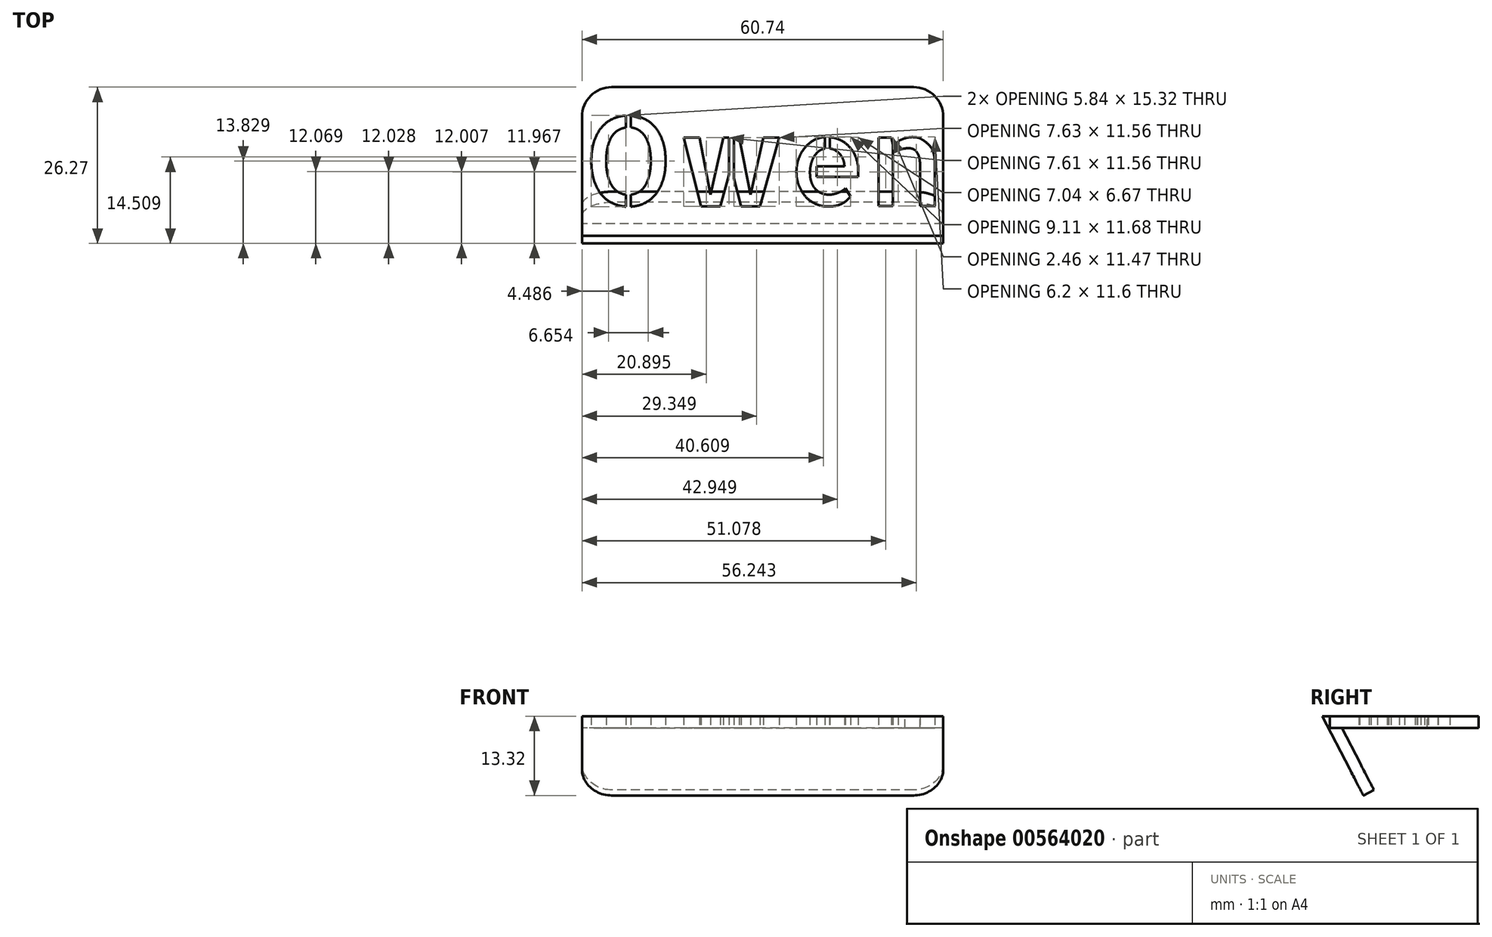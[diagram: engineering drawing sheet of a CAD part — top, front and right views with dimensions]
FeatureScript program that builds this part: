
annotation { "Feature Type Name" : "Feature", "Feature Type Description" : "" }
export const myFeature = defineFeature(function(context is Context, id is Id, definition is map)
    precondition{}
    {
        {
            var Q0;
            Q0=qCreatedBy(makeId("Top.planeOp"),FACE);
            var sketch = newSketch(context, id + "F0", { "sketchPlane" : qUnion([Q0])});
            skLineSegment(sketch, "E0.bottom", {"start": v(-23.58, 12.5) * mm, "end": v(37.16, 12.5) * mm});
            skLineSegment(sketch, "E0.top", {"start": v(-23.58, -12.5) * mm, "end": v(37.16, -12.5) * mm});
            skLineSegment(sketch, "E0.left", {"start": v(-23.58, 12.5) * mm, "end": v(-23.58, -12.5) * mm});
            skLineSegment(sketch, "E0.right", {"start": v(37.16, 12.5) * mm, "end": v(37.16, -12.5) * mm});
            skText(sketch, "E1", { "text": "Owen", "fontName": "AllertaStencil-Regular.ttf"});
            const initialGuessF0  = {"E1": [-0.02358, -0.0075, 1, 0, 0.015]};
            skSetInitialGuess(sketch, initialGuessF0);
            skSolve(sketch);
        }
        {
            var Q0;
            Q0=makeQuery(id+"F0.imprint","IMPRINT",FACE,{"disambiguationData":[TD([[makeQuery(id+"F0.imprint","IMPRINT",EDGE,{"derivedFrom":sQuery(id+"F0.wireOp",EDGE,"E0.bottom")}),-1.0]])]});
            extrude(context, id + "F1", {"entities" : qUnion([Q0]), "depth" : 2 * mm, "offsetDistance" : 25 * mm});
        }
        {
            var Q0;
            {var subQ0=sQuery(id+"F0.wireOp",EDGE,"E0.left");Q0=makeQuery(id+"FYEOEdhl7jzHk82_2.opBoolean","MERGE",FACE,{"derivedFrom":[makeQuery(id+"F1.opExtrude","SWEPT_FACE",FACE,{"disambiguationData":[OSD([subQ0])]}),makeQuery(id+"FOv1BJgTRWeWuMw_1.opExtrude","CAP_FACE",FACE,{"disambiguationData":[OSD([sQuery(id+"F0.wireOp",EDGE,"E0.bottom"),subQ0,sQuery(id+"Fjco5yBOxZZxTCI_1.wireOp",EDGE,"TpTMtmOo-qoIM-rLEy-p7IH-mKgsBanMGF23"),sQuery(id+"Fjco5yBOxZZxTCI_1.wireOp",EDGE,"Ja6BvVoQ-cpFi-Lcom-cL8s-5xC4kZiynyNl"),sQuery(id+"Fjco5yBOxZZxTCI_1.wireOp",EDGE,"utNyaJ8P-FD6r-AD7x-tpFW-fHytfVhziHLl"),sQuery(id+"Fjco5yBOxZZxTCI_1.wireOp",EDGE,"xGzW29bi-H5H8-ObLh-gdKj-mSPkAtMAUUzO")])],"isStart":true})]});}
            var sketch = newSketch(context, id + "F2", { "sketchPlane" : qUnion([Q0])});
            skLineSegment(sketch, "E2", {"start": v(11.52, 2) * mm, "end": v(5.09, -10.4) * mm});
            skLineSegment(sketch, "E3", {"start": v(5.09, -10.4) * mm, "end": v(6.87, -11.32) * mm});
            skLineSegment(sketch, "E4", {"start": v(6.87, -11.32) * mm, "end": v(13.77, 2) * mm});
            skLineSegment(sketch, "E5", {"start": v(13.77, 2) * mm, "end": v(11.52, 2) * mm});
            skSolve(sketch);
        }
        {
            var Q0;
            {var subQ4=sQuery(id+"F2.wireOp",EDGE,"E3");Q0=makeQuery(id+"F2.imprint","IMPRINT",FACE,{"disambiguationData":[TD([[makeQuery(id+"F2.imprint","IMPRINT",EDGE,{"derivedFrom":subQ4}),1.0]])]});}
            var Q1;
            Q1=makeQuery(id+"F1.opExtrude","SWEPT_FACE",FACE,{"disambiguationData":[OSD([sQuery(id+"F0.wireOp",EDGE,"E0.right")])]});
            extrude(context, id + "F3", {"entities" : qUnion([Q0]), "endBound" : BoundingType.UP_TO_SURFACE, "oppositeDirection" : true, "depth" : 75 * mm, "endBoundEntityFace" : qUnion([Q1]), "offsetDistance" : 25 * mm});
        }
        {
            var Q0;
            Q0=makeQuery(id+"F1.opExtrude","SWEPT_EDGE",EDGE,{"disambiguationData":[OSD([sQuery(id+"F0.wireOp",EDGE,"E0.bottom"),sQuery(id+"F0.wireOp",EDGE,"E0.left")])]});
            var Q1;
            Q1=makeQuery(id+"F1.opExtrude","SWEPT_EDGE",EDGE,{"disambiguationData":[OSD([sQuery(id+"F0.wireOp",EDGE,"E0.bottom"),sQuery(id+"F0.wireOp",EDGE,"E0.right")])]});
            var Q2;
            Q2=makeQuery(id+"F3.opExtrude","CAP_EDGE",EDGE,{"disambiguationData":[OSD([sQuery(id+"F2.wireOp",EDGE,"E3")])],"isStart":false});
            var Q3;
            Q3=makeQuery(id+"F3.opExtrude","CAP_EDGE",EDGE,{"disambiguationData":[OSD([sQuery(id+"F2.wireOp",EDGE,"E3")])],"isStart":true});
            var Q4;
            Q4=makeQuery(id+"F3.opExtrude","TWEAK_EDGE",EDGE,{"derivedFrom":[makeQuery(id+"F1.opExtrude","SWEPT_FACE",FACE,{"disambiguationData":[OSD([sQuery(id+"F0.wireOp",EDGE,"E0.right")])]}),makeQuery(id+"F2.imprint","IMPRINT",EDGE,{"derivedFrom":sQuery(id+"F2.wireOp",EDGE,"E3")})]});
            fillet(context, id + "F4", {"entities" : qUnion([Q0, Q1, Q2, Q3, Q4]), "radius" : 5 * mm, "tangentPropagation" : true, "allowEdgeOverflow" : false});
        }
    });
